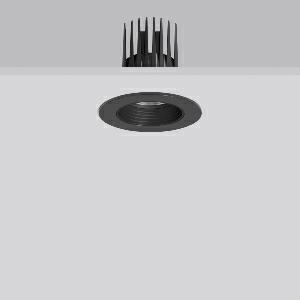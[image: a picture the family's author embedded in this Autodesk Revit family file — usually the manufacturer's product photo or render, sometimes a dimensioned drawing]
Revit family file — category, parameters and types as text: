
# Revit family: heledon_mini_e_901754_003_6eba
name_source: partatom
category: Lighting Fixtures
units: mm (PartAtom-declared; Revit-internal decimal feet)

## family parameters
Cut with Voids When Loaded = No
Host = Face
Light Source = No
Part Type = Normal
Room Calculation Point = No
Round Connector Dimension = Use Diameter
Shared = No

## types (1)
- HELEDON mini E (1 x LED Modul 930, 3250 lm, 3000)
    Apparent Load = 29 VA
    Approval mark = CE
    CIE Flux Codes = 80 99 100 100 100
    Color Rendering = 90
    Color Temperature = 3000
    Default Elevation = 1800 mm
    Description = Series: HELEDON mini
Round recessed downlight. Housing: die-cast aluminium, powder-coated. Black plastic ring and recessed LED to prevent glare from the side. Optical assembly with lens made of plastic (polycarbonate) for the best homogeneous light distribution - can be changed without tools. Best colour rendering index Ra>90. Suitable for Recessed ceiling mounting. Installation without tools thanks to spring fastening system. Including separate LED converter with connecting cable 600 mm.High quality converter without flickering and stroboscopic effect. Through-wiring box (5 pole) available as accessory. The following accessories can be mounted without use of tools: interchangeable lenses, decorative glasses, honeycomb louvre, clear and frosted diffusers, white interchangeable plastic ring. 
Colour: deep black, matt (RAL 9005)
Diameter: 124 mm
Height: 3 mm
Cut-out diameter: 114 mm
Recess height: 170 mm
Luminaire: recess height: 120 mm
Lamp: LED
Socket: without socket
Colour temperature: 3000K
Colour rendering index (CRI): 92
System power: 29 W
Rated luminous flux: 3250 lm
Luminous efficiency: 112 lm/W
Control gear: Regulated power supply
Protection class: II
Type of protection: IP 20
    Height = 0 mm  [stored 0 ft]
    Lamp = 1 x LED Modul 930
    Lamp Light Flux = 3250 lm
    Lamp count = 1
    Length = 124 mm  [stored 0.406824 ft]
    Lifetime = 50000 h
    Luminous efficacy = 112 lm/W
    Manufacturer = RZB
    ModVariant = No
    Model = 901754.003
    Mounting Place = Ceiling
    Mounting Type = Recessed
    Number of Poles = 1
    OnlyDefault = Yes
    Power Factor = 1
    Product Name = HELEDON mini E
    Product group = Recessed downlights
    ProductGroupID = 402
    Protection Class = Protection class II
    Protection Degree = IP 20
    RLX_Detail_Level = 1
    RLX_Emergency_Light_Flux = 0 lm
    RLX_Emergency_Type = 0
    RLX_Emergency_Type_DB = No
    RlxData = <blob elided: 128797 chars, md5=73478344>
    Socket = socket
    Standby Power = 0 W
    System Light Flux = 3250 lm
    System Power = 29 W
    Type Comments = Product without accessories
    Type Image = 901656.003.jpg
    URL = http://relux.com
    VarID = ---
    Voltage = 230 V
    Voltage Range = 220-240 V
    Weight = 0.00 kg
    Width = 0 mm  [stored 0 ft]

note: [stored X ft] marks values corroborated as IEEE doubles in the binary element streams (Revit-internal decimal feet)

## geometry (parser evidence)
native form markers: Blend x4, Sweep x12
no freeform markers — native parametric forms only
